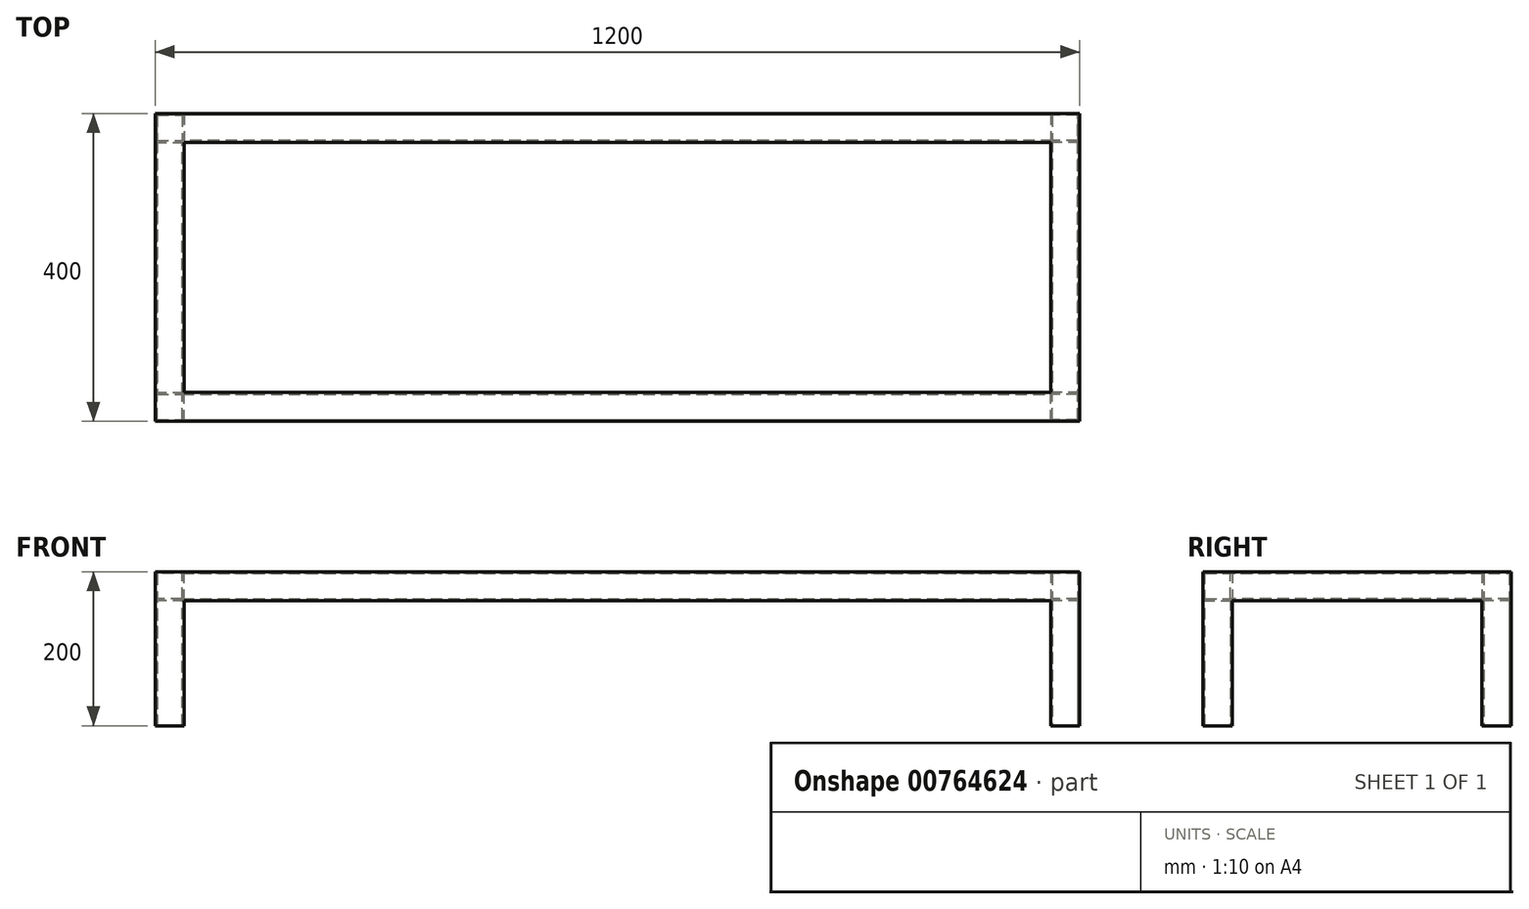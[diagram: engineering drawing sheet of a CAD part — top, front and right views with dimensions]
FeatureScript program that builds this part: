
annotation { "Feature Type Name" : "Feature", "Feature Type Description" : "" }
export const myFeature = defineFeature(function(context is Context, id is Id, definition is map)
    precondition{}
    {
        {
            var Q0;
            Q0=qCreatedBy(makeId("Front.planeOp"),FACE);
            var sketch = newSketch(context, id + "F0", { "sketchPlane" : qUnion([Q0])});
            skLineSegment(sketch, "E0.bottom", {"start": v(0, 0) * mm, "end": v(38, 0) * mm});
            skLineSegment(sketch, "E0.top", {"start": v(0, 200) * mm, "end": v(38, 200) * mm});
            skLineSegment(sketch, "E0.left", {"start": v(0, 0) * mm, "end": v(0, 200) * mm});
            skLineSegment(sketch, "E0.right", {"start": v(38, 0) * mm, "end": v(38, 162) * mm});
            skLineSegment(sketch, "E1.bottom", {"start": v(38, 200) * mm, "end": v(1200, 200) * mm});
            skLineSegment(sketch, "E1.top", {"start": v(38, 162) * mm, "end": v(1162, 162) * mm});
            skLineSegment(sketch, "E2.bottom", {"start": v(1200, 200) * mm, "end": v(1162, 200) * mm});
            skLineSegment(sketch, "E2.top", {"start": v(1200, 0) * mm, "end": v(1162, 0) * mm});
            skLineSegment(sketch, "E2.left", {"start": v(1200, 200) * mm, "end": v(1200, 0) * mm});
            skLineSegment(sketch, "E2.right", {"start": v(1162, 162) * mm, "end": v(1162, 0) * mm});
            skSolve(sketch);
        }
        {
            var Q0;
            Q0 = qSketchRegion(id + "F0", true);
            extrude(context, id + "F1", {"entities" : qUnion([Q0]), "depth" : 38 * mm, "offsetDistance" : 25 * mm});
        }
        {
            var Q0;
            Q0=makeQuery(id+"F1.opExtrude","SWEPT_FACE",FACE,{"disambiguationData":[OSD([sQuery(id+"F0.wireOp",EDGE,"E0.left")])]});
            var sketch = newSketch(context, id + "F2", { "sketchPlane" : qUnion([Q0])});
            skLineSegment(sketch, "E3", {"start": v(0, 200) * mm, "end": v(-324, 200) * mm});
            skLineSegment(sketch, "E4", {"start": v(-324, 200) * mm, "end": v(-324, 162) * mm});
            skLineSegment(sketch, "E5", {"start": v(-324, 162) * mm, "end": v(0, 162) * mm});
            skSolve(sketch);
        }
        {
            var Q0;
            Q0 = qSketchRegion(id + "F2", true);
            var Q1;
            {var subQ0=sQuery(id+"F2.wireOp",EDGE,"E3");Q1=makeQuery(id+"F2.imprint","IMPRINT",FACE,{"disambiguationData":[TD([[makeQuery(id+"F2.imprint","IMPRINT",EDGE,{"derivedFrom":subQ0}),1.0]])]});}
            extrude(context, id + "F3", {"entities" : qUnion([Q0, Q1]), "operationType" : NewBodyOperationType.ADD, "oppositeDirection" : true, "depth" : 38 * mm, "offsetDistance" : 25 * mm});
        }
        {
            var Q0;
            {var subQ0=sQuery(id+"F0.wireOp",EDGE,"E0.right");var subQ2=sQuery(id+"F0.wireOp",EDGE,"E2.bottom");var subQ3=sQuery(id+"F0.wireOp",EDGE,"E1.bottom");var subQ4=sQuery(id+"F0.wireOp",EDGE,"E0.top");var subQ6=sQuery(id+"F0.wireOp",EDGE,"E0.left");var subQ7=sQuery(id+"F0.wireOp",EDGE,"E1.top");var subQ8=sQuery(id+"F0.wireOp",EDGE,"E2.right");var subQ9=sQuery(id+"F0.wireOp",EDGE,"E2.left");var subQ10=sQuery(id+"F0.wireOp",EDGE,"E2.top");var subQ11=makeQuery(id+"F1.opExtrude","CAP_FACE",FACE,{"disambiguationData":[OSD([sQuery(id+"F0.wireOp",EDGE,"E0.bottom"),subQ4,subQ6,subQ0,subQ3,subQ7,subQ2,subQ10,subQ9,subQ8])],"isStart":true});Q0=makeQuery(id+"F3.boolean.opBoolean","SPLIT",FACE,{"disambiguationData":[TD([makeQuery(id+"F1.opExtrude","SWEPT_FACE",FACE,{"disambiguationData":[OSD([subQ10])]})])],"derivedFrom":subQ11});}
            var sketch = newSketch(context, id + "F4", { "sketchPlane" : qUnion([Q0])});
            skLineSegment(sketch, "E6.bottom", {"start": v(-1200, 200) * mm, "end": v(-1162, 200) * mm});
            skLineSegment(sketch, "E6.top", {"start": v(-1200, 162) * mm, "end": v(-1162, 162) * mm});
            skLineSegment(sketch, "E6.left", {"start": v(-1200, 200) * mm, "end": v(-1200, 162) * mm});
            skLineSegment(sketch, "E6.right", {"start": v(-1162, 200) * mm, "end": v(-1162, 162) * mm});
            skSolve(sketch);
        }
        {
            var Q0;
            Q0 = qSketchRegion(id + "F4", true);
            extrude(context, id + "F5", {"entities" : qUnion([Q0]), "operationType" : NewBodyOperationType.ADD, "depth" : 324 * mm, "offsetDistance" : 25 * mm});
        }
        {
            var Q0;
            Q0=makeQuery(id+"F5.opExtrude","CAP_FACE",FACE,{"disambiguationData":[OSD([sQuery(id+"F4.wireOp",EDGE,"E6.bottom"),sQuery(id+"F4.wireOp",EDGE,"E6.top"),sQuery(id+"F4.wireOp",EDGE,"E6.left"),sQuery(id+"F4.wireOp",EDGE,"E6.right")])],"isStart":false});
            var sketch = newSketch(context, id + "F6", { "sketchPlane" : qUnion([Q0])});
            skLineSegment(sketch, "E7.bottom", {"start": v(-1200, 200) * mm, "end": v(0, 200) * mm});
            skLineSegment(sketch, "E7.top", {"start": v(-1162, 162) * mm, "end": v(-38, 162) * mm});
            skLineSegment(sketch, "E7.left", {"start": v(-1200, 200) * mm, "end": v(-1200, 162) * mm});
            skLineSegment(sketch, "E7.right", {"start": v(0, 200) * mm, "end": v(0, 162) * mm});
            skLineSegment(sketch, "E8.bottom", {"start": v(-1200, 200) * mm, "end": v(-1162, 200) * mm});
            skLineSegment(sketch, "E8.top", {"start": v(-1200, 0) * mm, "end": v(-1162, 0) * mm});
            skLineSegment(sketch, "E8.left", {"start": v(-1200, 200) * mm, "end": v(-1200, 0) * mm});
            skLineSegment(sketch, "E8.right", {"start": v(-1162, 162) * mm, "end": v(-1162, 0) * mm});
            skLineSegment(sketch, "E9.bottom", {"start": v(0, 200) * mm, "end": v(-38, 200) * mm});
            skLineSegment(sketch, "E9.top", {"start": v(0, 0) * mm, "end": v(-38, 0) * mm});
            skLineSegment(sketch, "E9.left", {"start": v(0, 200) * mm, "end": v(0, 0) * mm});
            skLineSegment(sketch, "E9.right", {"start": v(-38, 162) * mm, "end": v(-38, 0) * mm});
            skSolve(sketch);
        }
        {
            var Q0;
            Q0 = qSketchRegion(id + "F6", true);
            extrude(context, id + "F7", {"entities" : qUnion([Q0]), "operationType" : NewBodyOperationType.ADD, "depth" : 38 * mm, "offsetDistance" : 25 * mm});
        }
        {
            var Q0;
            Q0=makeQuery(id+"F7.opExtrude","SWEPT_FACE",FACE,{"disambiguationData":[OSD([sQuery(id+"F6.wireOp",EDGE,"E9.top")])]});
            var Q1;
            Q1=makeQuery(id+"F1.opExtrude","SWEPT_FACE",FACE,{"disambiguationData":[OSD([sQuery(id+"F0.wireOp",EDGE,"E0.bottom")])]});
            var Q2;
            Q2=makeQuery(id+"F1.opExtrude","SWEPT_FACE",FACE,{"disambiguationData":[OSD([sQuery(id+"F0.wireOp",EDGE,"E2.top")])]});
            var Q3;
            Q3=makeQuery(id+"F7.opExtrude","SWEPT_FACE",FACE,{"disambiguationData":[OSD([sQuery(id+"F6.wireOp",EDGE,"E8.top")])]});
            shell(context, id + "F8", {"entities" : qUnion([Q0, Q1, Q2, Q3]), "thickness" : 2.5 * mm});
        }
    });
